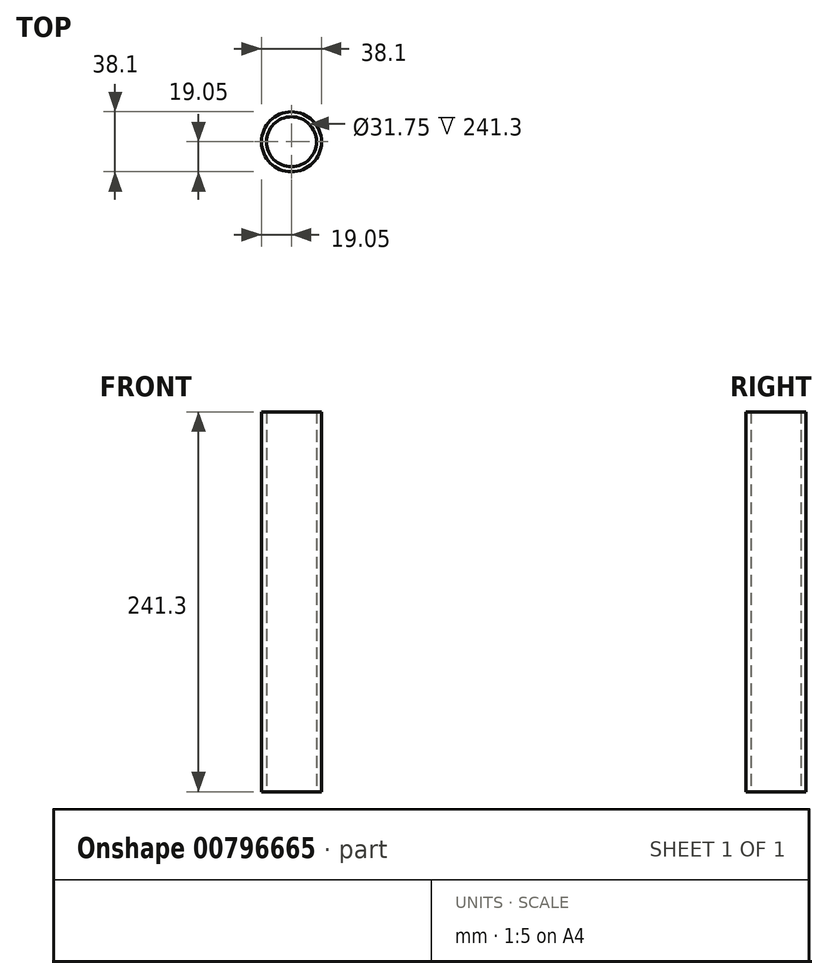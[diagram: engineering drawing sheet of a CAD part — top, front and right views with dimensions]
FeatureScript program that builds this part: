
annotation { "Feature Type Name" : "Feature", "Feature Type Description" : "" }
export const myFeature = defineFeature(function(context is Context, id is Id, definition is map)
    precondition{}
    {
        {
            var Q0;
            Q0=qCreatedBy(makeId("Top.planeOp"),FACE);
            var sketch = newSketch(context, id + "F0", { "sketchPlane" : qUnion([Q0])});
            skCircle(sketch, "E0", {"center": v(0, 0) * mm, "radius": 19.05 * mm});
            skCircle(sketch, "E1", {"center": v(0, 0) * mm, "radius": 15.88 * mm});
            skSolve(sketch);
        }
        {
            var Q0;
            Q0 = qSketchRegion(id + "F0", true);
            extrude(context, id + "F1", {"entities" : qUnion([Q0]), "depth" : 241.3 * mm, "offsetDistance" : 25.4 * mm});
        }
    });
